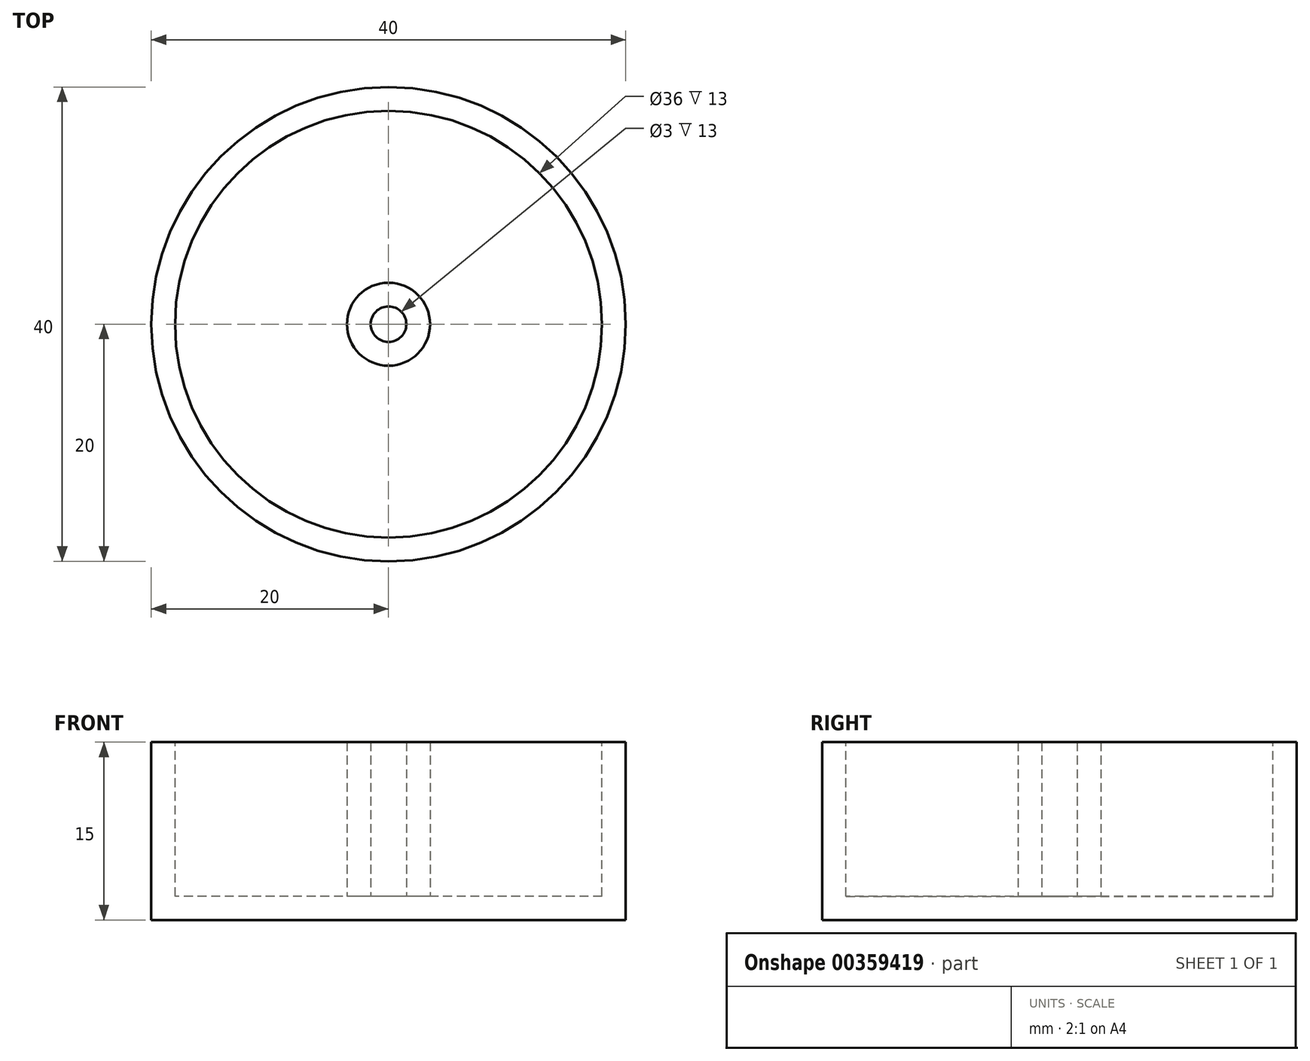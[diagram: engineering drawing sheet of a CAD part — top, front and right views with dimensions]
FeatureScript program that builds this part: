
annotation { "Feature Type Name" : "Feature", "Feature Type Description" : "" }
export const myFeature = defineFeature(function(context is Context, id is Id, definition is map)
    precondition{}
    {
        {
            var Q0;
            Q0=qCreatedBy(makeId("Top.planeOp"),FACE);
            var sketch = newSketch(context, id + "F0", { "sketchPlane" : qUnion([Q0])});
            skCircle(sketch, "E0", {"center": v(0, 0) * mm, "radius": 20 * mm});
            skSolve(sketch);
        }
        {
            var Q0;
            Q0 = qSketchRegion(id + "F0", true);
            extrude(context, id + "F1", {"entities" : qUnion([Q0]), "depth" : 15 * mm});
        }
        {
            var Q0;
            Q0=makeQuery(id+"F1.opExtrude","CAP_FACE",FACE,{"disambiguationData":[OSD([sQuery(id+"F0.wireOp",EDGE,"E0")])],"isStart":false});
            var sketch = newSketch(context, id + "F2", { "sketchPlane" : qUnion([Q0])});
            skCircle(sketch, "E1", {"center": v(0, 0) * mm, "radius": 18 * mm});
            skSolve(sketch);
        }
        {
            var Q0;
            Q0=makeQuery(id+"F2.imprint","IMPRINT",FACE,{"disambiguationData":[TD([[makeQuery(id+"F2.imprint","IMPRINT",EDGE,{"derivedFrom":sQuery(id+"F2.wireOp",EDGE,"E1")}),1.0]])]});
            extrude(context, id + "F3", {"entities" : qUnion([Q0]), "operationType" : NewBodyOperationType.REMOVE, "oppositeDirection" : true, "depth" : 13 * mm});
        }
        {
            var Q0;
            Q0=makeQuery(id+"F3.boolean.opBoolean","COPY",FACE,{"derivedFrom":makeQuery(id+"F3.opExtrude","CAP_FACE",FACE,{"disambiguationData":[OSD([sQuery(id+"F2.wireOp",EDGE,"E1")])],"isStart":false})});
            var sketch = newSketch(context, id + "F4", { "sketchPlane" : qUnion([Q0])});
            skCircle(sketch, "E2", {"center": v(0, 0) * mm, "radius": 3.5 * mm});
            skCircle(sketch, "E3", {"center": v(0, 0) * mm, "radius": 1.5 * mm});
            skSolve(sketch);
        }
        {
            var Q0;
            Q0=makeQuery(id+"F4.imprint","IMPRINT",FACE,{"disambiguationData":[TD([[makeQuery(id+"F4.imprint","IMPRINT",EDGE,{"derivedFrom":sQuery(id+"F4.wireOp",EDGE,"E2")}),1.0]])]});
            extrude(context, id + "F5", {"entities" : qUnion([Q0]), "operationType" : NewBodyOperationType.ADD, "depth" : 13 * mm});
        }
    });
